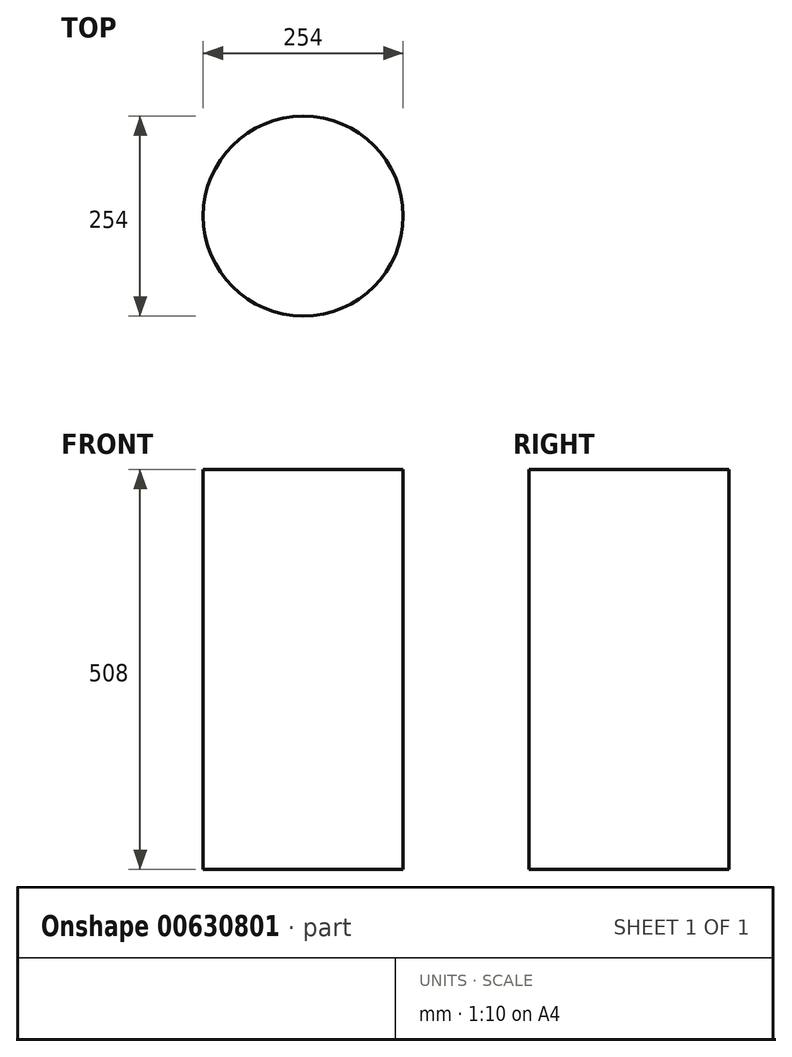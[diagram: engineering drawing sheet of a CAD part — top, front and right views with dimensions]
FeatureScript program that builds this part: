
annotation { "Feature Type Name" : "Feature", "Feature Type Description" : "" }
export const myFeature = defineFeature(function(context is Context, id is Id, definition is map)
    precondition{}
    {
        {
            var Q0;
            Q0=qCreatedBy(makeId("Top.planeOp"),FACE);
            var sketch = newSketch(context, id + "F0", { "sketchPlane" : qUnion([Q0])});
            skCircle(sketch, "E0", {"center": v(0, 0) * mm, "radius": 127 * mm});
            skSolve(sketch);
        }
        {
            var Q0;
            Q0 = qSketchRegion(id + "F0", true);
            extrude(context, id + "F1", {"entities" : qUnion([Q0]), "endBound" : BoundingType.SYMMETRIC, "depth" : 508 * mm, "offsetDistance" : 25.4 * mm});
        }
    });
